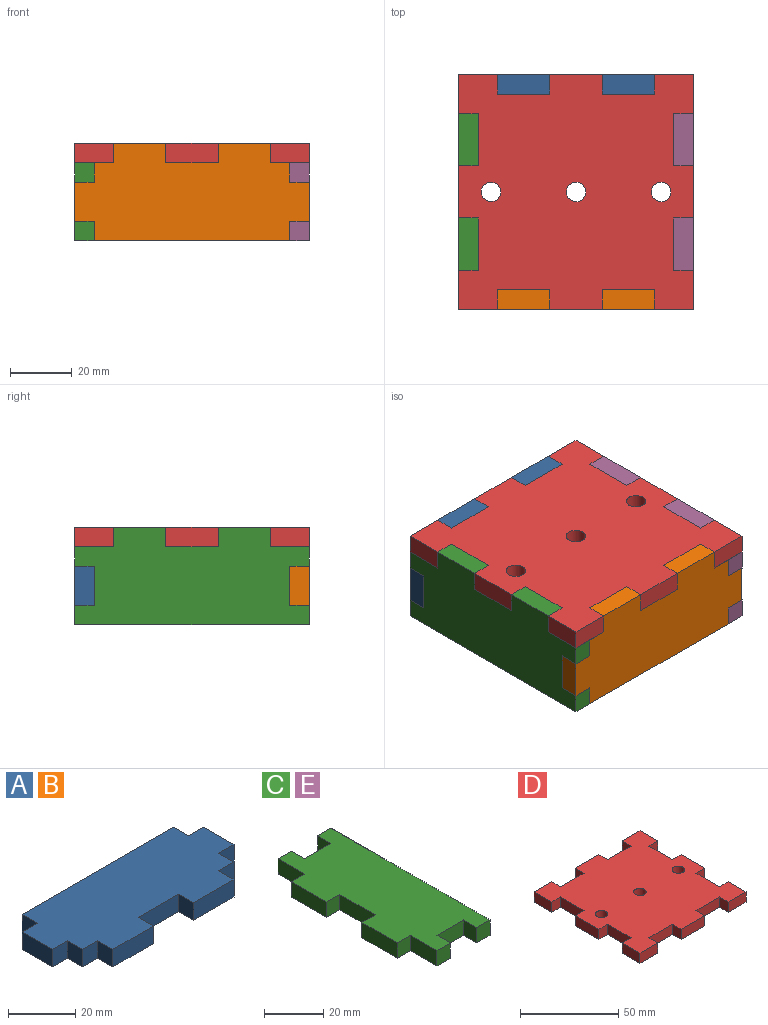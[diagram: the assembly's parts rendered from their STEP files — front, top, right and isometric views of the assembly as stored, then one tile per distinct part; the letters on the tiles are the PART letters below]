
ASSEMBLY  parts=5 mates=4
PART A: 22 faces, bbox 76.2x31.8x6.4 mm
  f0: plane 6.35x6.35mm, normal (1,0,0), area 40.3mm2, adj f1,f19,f20,f21
  f1: plane 6.35x6.35mm, normal (0,-1,0), area 40.3mm2, adj f0,f2,f20,f21
  f2: plane 6.35x6.35mm, normal (1,0,0), area 40.3mm2, adj f1,f3,f20,f21
  f3: plane 6.35x6.35mm, normal (0,-1,0), area 40.3mm2, adj f2,f4,f20,f21
  f4: plane 12.7x6.35mm, normal (1,0,0), area 80.6mm2, adj f3,f5,f20,f21
  f5: plane 6.35x6.35mm, normal (0,1,0), area 40.3mm2, adj f4,f6,f20,f21
  f6: plane 6.35x6.35mm, normal (1,0,0), area 40.3mm2, adj f5,f7,f20,f21
  f7: plane 63.5x6.35mm, normal (0,1,0), area 403.2mm2, adj f6,f8,f20,f21
  f8: plane 6.35x6.35mm, normal (-1,0,0), area 40.3mm2, adj f7,f9,f20,f21
  f9: plane 6.35x6.35mm, normal (0,1,0), area 40.3mm2, adj f8,f10,f20,f21
  f10: plane 12.7x6.35mm, normal (-1,0,0), area 80.6mm2, adj f9,f11,f20,f21
  f11: plane 6.35x6.35mm, normal (0,-1,0), area 40.3mm2, adj f10,f12,f20,f21
  f12: plane 6.35x6.35mm, normal (-1,0,0), area 40.3mm2, adj f11,f13,f20,f21
  f13: plane 6.35x6.35mm, normal (0,-1,0), area 40.3mm2, adj f12,f14,f20,f21
  f14: plane 6.35x6.35mm, normal (-1,0,0), area 40.3mm2, adj f13,f15,f20,f21
  f15: plane 16.93x6.35mm, normal (0,-1,0), area 107.5mm2, adj f14,f16,f20,f21
  f16: plane 6.35x6.35mm, normal (1,0,0), area 40.3mm2, adj f15,f17,f20,f21
  f17: plane 16.93x6.35mm, normal (0,-1,0), area 107.5mm2, adj f16,f18,f20,f21
  f18: plane 6.35x6.35mm, normal (-1,0,0), area 40.3mm2, adj f17,f19,f20,f21
  f19: plane 16.93x6.35mm, normal (0,-1,0), area 107.5mm2, adj f0,f18,f20,f21
  f20: plane 76.2x31.75mm, normal (0,0,1), area 1989.2mm2, adj f0,f1,f2,f3,f4,f5,f6,f7
  f21: plane 76.2x31.75mm, normal (0,0,-1), area 1989.2mm2, adj f0,f1,f2,f3,f4,f5,f6,f7
PART B: same geometry as A
PART C: 22 faces, bbox 31.8x76.2x6.4 mm
  f0: plane 12.7x6.35mm, normal (0,1,0), area 80.6mm2, adj f1,f19,f20,f21
  f1: plane 6.35x6.35mm, normal (1,0,0), area 40.3mm2, adj f0,f2,f20,f21
  f2: plane 6.35x6.35mm, normal (0,1,0), area 40.3mm2, adj f1,f3,f20,f21
  f3: plane 12.7x6.35mm, normal (-1,0,0), area 80.6mm2, adj f2,f4,f20,f21
  f4: plane 6.35x6.35mm, normal (0,1,0), area 40.3mm2, adj f3,f5,f20,f21
  f5: plane 16.93x6.35mm, normal (-1,0,0), area 107.5mm2, adj f4,f6,f20,f21
  f6: plane 6.35x6.35mm, normal (0,-1,0), area 40.3mm2, adj f5,f7,f20,f21
  f7: plane 16.93x6.35mm, normal (-1,0,0), area 107.5mm2, adj f6,f8,f20,f21
  f8: plane 6.35x6.35mm, normal (0,1,0), area 40.3mm2, adj f7,f9,f20,f21
  f9: plane 16.93x6.35mm, normal (-1,0,0), area 107.5mm2, adj f8,f10,f20,f21
  f10: plane 6.35x6.35mm, normal (0,-1,0), area 40.3mm2, adj f9,f11,f20,f21
  f11: plane 12.7x6.35mm, normal (-1,0,0), area 80.6mm2, adj f10,f12,f20,f21
  f12: plane 6.35x6.35mm, normal (0,-1,0), area 40.3mm2, adj f11,f13,f20,f21
  f13: plane 6.35x6.35mm, normal (1,0,0), area 40.3mm2, adj f12,f14,f20,f21
  f14: plane 12.7x6.35mm, normal (0,-1,0), area 80.6mm2, adj f13,f15,f20,f21
  f15: plane 6.35x6.35mm, normal (-1,0,0), area 40.3mm2, adj f14,f16,f20,f21
  f16: plane 6.35x6.35mm, normal (0,-1,0), area 40.3mm2, adj f15,f17,f20,f21
  f17: plane 76.2x6.35mm, normal (1,0,0), area 483.9mm2, adj f16,f18,f20,f21
  f18: plane 6.35x6.35mm, normal (0,1,0), area 40.3mm2, adj f17,f19,f20,f21
  f19: plane 6.35x6.35mm, normal (-1,0,0), area 40.3mm2, adj f0,f18,f20,f21
  f20: plane 76.2x31.75mm, normal (0,0,1), area 1989.2mm2, adj f0,f1,f2,f3,f4,f5,f6,f7
  f21: plane 76.2x31.75mm, normal (0,0,-1), area 1989.2mm2, adj f0,f1,f2,f3,f4,f5,f6,f7
PART D: 41 faces, bbox 76.2x76.2x6.4 mm
  f0: plane 12.7x6.35mm, normal (1,0,0), area 80.6mm2, adj f1,f38,f39,f40
  f1: plane 12.7x6.35mm, normal (0,1,0), area 80.6mm2, adj f0,f2,f39,f40
  f2: plane 6.35x6.35mm, normal (-1,0,0), area 40.3mm2, adj f1,f3,f39,f40
  f3: plane 16.93x6.35mm, normal (0,1,0), area 107.5mm2, adj f2,f4,f39,f40
  f4: plane 6.35x6.35mm, normal (1,0,0), area 40.3mm2, adj f3,f5,f39,f40
  f5: plane 16.93x6.35mm, normal (0,1,0), area 107.5mm2, adj f4,f6,f39,f40
  f6: plane 6.35x6.35mm, normal (-1,0,0), area 40.3mm2, adj f5,f7,f39,f40
  f7: plane 16.93x6.35mm, normal (0,1,0), area 107.5mm2, adj f6,f8,f39,f40
  f8: plane 6.35x6.35mm, normal (1,0,0), area 40.3mm2, adj f7,f9,f39,f40
  f9: plane 12.7x6.35mm, normal (0,1,0), area 80.6mm2, adj f8,f10,f39,f40
  f10: plane 12.7x6.35mm, normal (-1,0,0), area 80.6mm2, adj f9,f11,f39,f40
  f11: plane 6.35x6.35mm, normal (0,-1,0), area 40.3mm2, adj f10,f12,f39,f40
  f12: plane 16.93x6.35mm, normal (-1,0,0), area 107.5mm2, adj f11,f13,f39,f40
  f13: plane 6.35x6.35mm, normal (0,1,0), area 40.3mm2, adj f12,f14,f39,f40
  f14: plane 16.93x6.35mm, normal (-1,0,0), area 107.5mm2, adj f13,f15,f39,f40
  f15: plane 6.35x6.35mm, normal (0,-1,0), area 40.3mm2, adj f14,f16,f39,f40
  f16: plane 16.93x6.35mm, normal (-1,0,0), area 107.5mm2, adj f15,f17,f39,f40
  f17: plane 6.35x6.35mm, normal (0,1,0), area 40.3mm2, adj f16,f18,f39,f40
  f18: plane 12.7x6.35mm, normal (-1,0,0), area 80.6mm2, adj f17,f19,f39,f40
  f19: plane 12.7x6.35mm, normal (0,-1,0), area 80.6mm2, adj f18,f20,f39,f40
  f20: plane 6.35x6.35mm, normal (1,0,0), area 40.3mm2, adj f19,f21,f39,f40
  f21: plane 16.93x6.35mm, normal (0,-1,0), area 107.5mm2, adj f20,f22,f39,f40
  f22: plane 6.35x6.35mm, normal (-1,0,0), area 40.3mm2, adj f21,f23,f39,f40
  f23: plane 16.93x6.35mm, normal (0,-1,0), area 107.5mm2, adj f22,f24,f39,f40
  f24: plane 6.35x6.35mm, normal (1,0,0), area 40.3mm2, adj f23,f25,f39,f40
  f25: plane 16.93x6.35mm, normal (0,-1,0), area 107.5mm2, adj f24,f26,f39,f40
  f26: plane 6.35x6.35mm, normal (-1,0,0), area 40.3mm2, adj f25,f27,f39,f40
  f27: plane 12.7x6.35mm, normal (0,-1,0), area 80.6mm2, adj f26,f28,f39,f40
  f28: plane 12.7x6.35mm, normal (1,0,0), area 80.6mm2, adj f27,f29,f39,f40
  f29: plane 6.35x6.35mm, normal (0,1,0), area 40.3mm2, adj f28,f30,f39,f40
  f30: plane 16.93x6.35mm, normal (1,0,0), area 107.5mm2, adj f29,f31,f39,f40
  f31: plane 6.35x6.35mm, normal (0,-1,0), area 40.3mm2, adj f30,f32,f39,f40
  f32: plane 16.93x6.35mm, normal (1,0,0), area 107.5mm2, adj f31,f33,f39,f40
  f33: plane 6.35x6.35mm, normal (0,1,0), area 40.3mm2, adj f32,f34,f39,f40
  f34: plane 16.93x6.35mm, normal (1,0,0), area 107.5mm2, adj f33,f38,f39,f40
  f35: cylinder r=3.17mm len=6.35mm, axis (0,0,-1), area 126.7mm2, adj f39,f40
  f36: cylinder r=3.17mm len=6.35mm, axis (0,0,-1), area 126.7mm2, adj f39,f40
  f37: cylinder r=3.17mm len=6.35mm, axis (0,0,-1), area 126.7mm2, adj f39,f40
  f38: plane 6.35x6.35mm, normal (0,-1,0), area 40.3mm2, adj f0,f34,f39,f40
  f39: plane 76.2x76.2mm, normal (0,0,1), area 4851.2mm2, adj f0,f1,f2,f3,f4,f5,f6,f7
  f40: plane 76.2x76.2mm, normal (0,0,-1), area 4851.2mm2, adj f0,f1,f2,f3,f4,f5,f6,f7
PART E: same geometry as C
PLACE A rot(axis=(-1,0,0),90deg) t=(3.61,33.41,59.69)mm
PLACE B rot(axis=(-1,0,0),90deg) t=(3.61,-36.44,59.69)mm
PLACE C rot(axis=(0,1,0),90deg) t=(-34.49,1.66,59.69)mm
PLACE D t=(3.61,1.66,-3.81)mm
PLACE E rot(axis=(0,1,0),90deg) t=(35.36,1.66,59.69)mm
MATE fastened B.f0 <-> D.f26  axis (1,0,0) through (29.01,-33.27,-0.64)mm
MATE fastened C.f10 <-> D.f17  axis (0,-1,0) through (-31.32,-23.74,-0.64)mm
MATE fastened E.f10 <-> D.f29  axis (0,-1,0) through (38.53,-23.74,-0.64)mm
MATE fastened A.f14 <-> D.f8  axis (-1,0,0) through (-21.79,36.58,-0.64)mm
